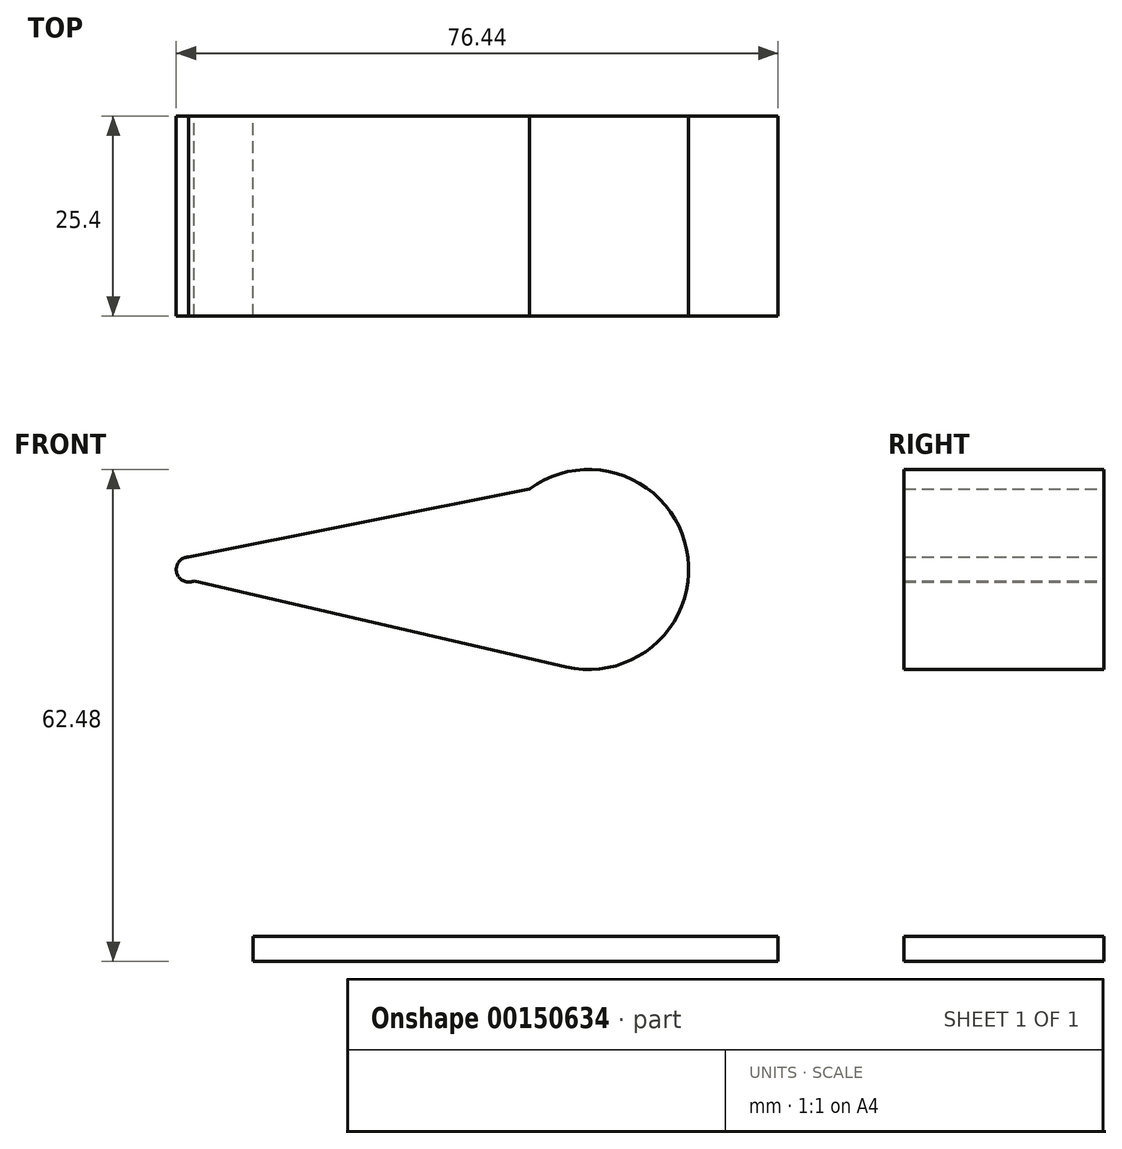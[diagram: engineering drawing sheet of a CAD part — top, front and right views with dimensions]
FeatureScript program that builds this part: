
annotation { "Feature Type Name" : "Feature", "Feature Type Description" : "" }
export const myFeature = defineFeature(function(context is Context, id is Id, definition is map)
    precondition{}
    {
        {
            var Q0;
            Q0=qCreatedBy(makeId("Front.planeOp"),FACE);
            var sketch = newSketch(context, id + "F0", { "sketchPlane" : qUnion([Q0])});
            skLineSegment(sketch, "E0.bottom", {"start": v(-31.8, -46.6) * mm, "end": v(34.88, -46.6) * mm});
            skLineSegment(sketch, "E0.top", {"start": v(-31.8, -49.78) * mm, "end": v(34.88, -49.78) * mm});
            skLineSegment(sketch, "E0.left", {"start": v(-31.8, -46.6) * mm, "end": v(-31.8, -49.78) * mm});
            skLineSegment(sketch, "E0.right", {"start": v(34.88, -46.6) * mm, "end": v(34.88, -49.78) * mm});
            skLineSegment(sketch, "E1.bottom", {"start": v(-29.83, -46.6) * mm, "end": v(-24.12, -46.6) * mm});
            skLineSegment(sketch, "E1.top", {"start": v(-29.83, -41.97) * mm, "end": v(-24.12, -41.97) * mm});
            skLineSegment(sketch, "E1.left", {"start": v(-29.83, -46.6) * mm, "end": v(-29.83, -41.97) * mm});
            skLineSegment(sketch, "E1.right", {"start": v(-24.12, -46.6) * mm, "end": v(-24.12, -41.97) * mm});
            skArc(sketch, "E2", {"start": v(7.97, -12.37) * mm, "mid": v(23.27, 2.55) * mm, "end": v(3.33, 10.25) * mm});
            skCircle(sketch, "E3", {"center": v(-39.97, 0) * mm, "radius": 1.59 * mm});
            skLineSegment(sketch, "E4", {"start": v(-39.97, 1.59) * mm, "end": v(3.33, 10.25) * mm});
            skLineSegment(sketch, "E5", {"start": v(-39.32, -1.45) * mm, "end": v(7.97, -12.37) * mm});
            skSolve(sketch);
        }
        {
            var Q0;
            Q0=makeQuery(id+"F0.imprint","IMPRINT",FACE,{"disambiguationData":[TD([[makeQuery(id+"F0.imprint","IMPRINT",EDGE,{"derivedFrom":sQuery(id+"F0.wireOp",EDGE,"E0.top")}),1.0]])]});
            var Q1;
            Q1=makeQuery(id+"F0.imprint","IMPRINT",FACE,{"disambiguationData":[TD([[makeQuery(id+"F0.imprint","IMPRINT",EDGE,{"derivedFrom":sQuery(id+"F0.wireOp",EDGE,"E1.bottom")}),1.0]])]});
            var Q2;
            {var subQ0=sQuery(id+"F0.wireOp",EDGE,"E3");var subQ1=makeQuery(id+"F0.imprint","INTERSECT",VERTEX,{"derivedFrom":[subQ0,sQuery(id+"F0.wireOp",EDGE,"E4")]});Q2=makeQuery(id+"F0.imprint","IMPRINT",FACE,{"disambiguationData":[TD([[makeQuery(id+"F0.imprint","IMPRINT",EDGE,{"disambiguationData":[TD([[subQ1,-1.0]])],"derivedFrom":subQ0}),1.0]])]});}
            var Q3;
            Q3=makeQuery(id+"F0.imprint","IMPRINT",FACE,{"disambiguationData":[TD([[makeQuery(id+"F0.imprint","IMPRINT",EDGE,{"derivedFrom":sQuery(id+"F0.wireOp",EDGE,"E2")}),1.0]])]});
            extrude(context, id + "F1", {"entities" : qUnion([Q0, Q1, Q2, Q3]), "depth" : 25.4 * mm});
        }
    });
